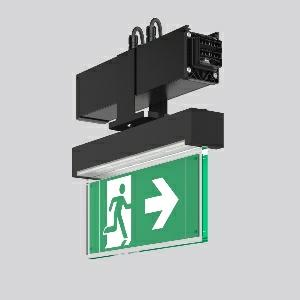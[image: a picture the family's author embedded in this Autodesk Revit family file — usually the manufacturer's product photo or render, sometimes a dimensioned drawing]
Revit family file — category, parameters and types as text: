
# Revit family: linedo_module_rz_9503rz_763_430_023_a5fc
name_source: partatom
category: Lighting Fixtures
units: mm (PartAtom-declared; Revit-internal decimal feet)

## family parameters
Cut with Voids When Loaded = No
Host = Face
Light Source = No
Part Type = Normal
Room Calculation Point = No
Round Connector Dimension = Use Diameter
Shared = No

## types (1)
- LINEDO Module RZ
    Apparent Load = 0 VA
    Default Elevation = 1800 mm
    Description = LINEDO, black, on/off
Continuous line luminaire, L 336 B 62 H 308, SBS, 3 h, automatischer Selbsttest
    Height = 308 mm
    Lamp = 0 x
    Length = 336 mm
    Luminous efficacy = 0 lm/W
    Manufacturer = RZB
    ModVariant = No
    Model = 9503RZ.763.430.023
    Mounting Place = Ceiling
    Mounting Type = Surface mounted
    Number of Poles = 1
    OnlyDefault = Yes
    Power Factor = 1
    Product Name = LINEDO Module RZ
    Product group = Continuous line luminaire system Linedo IP 54
    ProductGroupID = 314
    Protection Class = Protection class I
    Protection Degree = IP 54
    RLX_Detail_Level = 1
    RLX_Emergency_Light_Flux = 0 lm
    RLX_Emergency_Type = 0
    RLX_Emergency_Type_DB = No
    RlxData = <blob elided: 37381 chars, md5=e6e42aa4>
    Standby Power = 0 W
    System Light Flux = 0 lm
    System Power = 0 W
    Type Comments = Product without accessories
    Type Image = 9503rz.763.434.023.jpg
    URL = http://relux.com
    VarID = ---
    Voltage = 0 V
    Weight = 0.00 kg
    Width = 62 mm  [stored 0.203412 ft]

note: [stored X ft] marks values corroborated as IEEE doubles in the binary element streams (Revit-internal decimal feet)

## geometry (parser evidence)
native form markers: Blend x4, Sweep x11
no freeform markers — native parametric forms only
